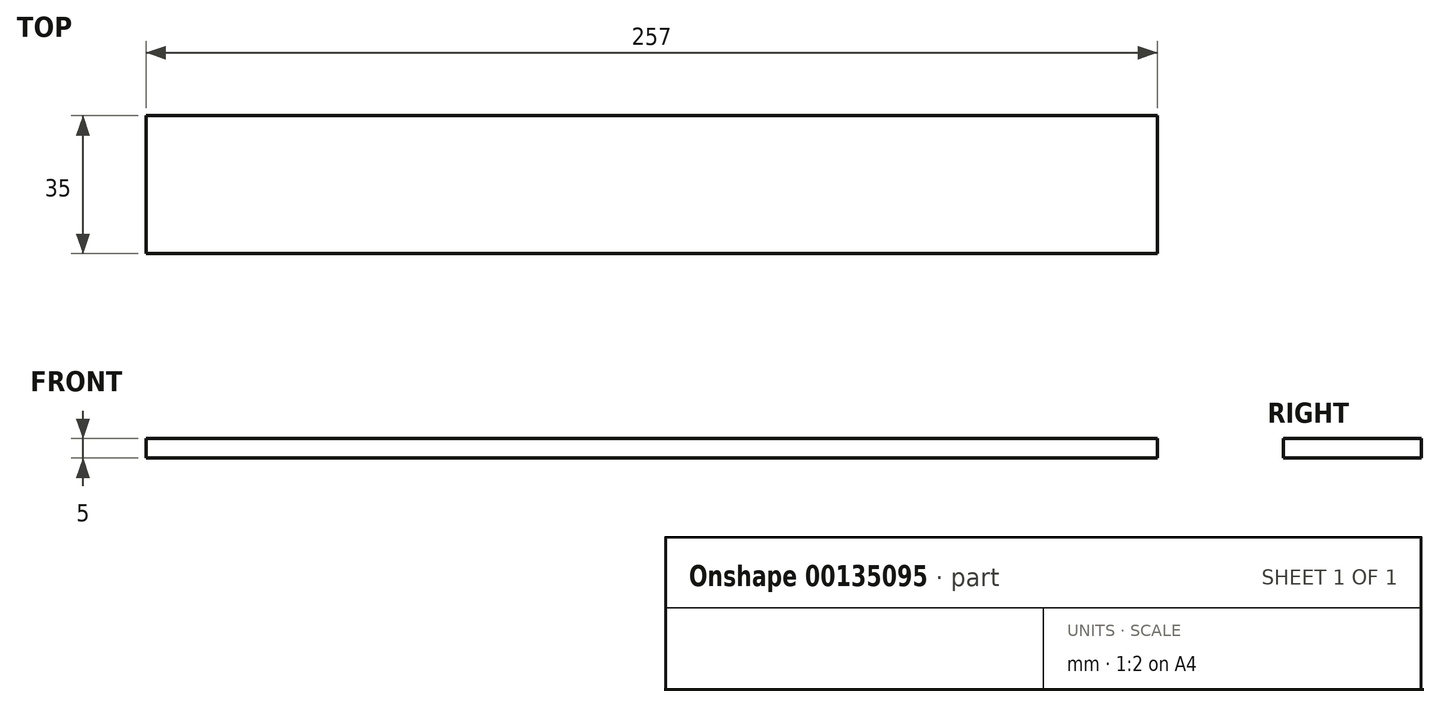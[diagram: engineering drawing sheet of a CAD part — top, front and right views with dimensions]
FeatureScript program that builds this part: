
annotation { "Feature Type Name" : "Feature", "Feature Type Description" : "" }
export const myFeature = defineFeature(function(context is Context, id is Id, definition is map)
    precondition{}
    {
        {
            var Q0;
            Q0=qCreatedBy(makeId("Top.planeOp"),FACE);
            var sketch = newSketch(context, id + "F0", { "sketchPlane" : qUnion([Q0])});
            skLineSegment(sketch, "E0.bottom", {"start": v(-76.55, 0) * mm, "end": v(220.45, 0) * mm});
            skLineSegment(sketch, "E0.top", {"start": v(-76.55, 35) * mm, "end": v(220.45, 35) * mm});
            skLineSegment(sketch, "E0.left", {"start": v(-76.55, 0) * mm, "end": v(-76.55, 35) * mm});
            skLineSegment(sketch, "E0.right", {"start": v(220.45, 0) * mm, "end": v(220.45, 35) * mm});
            skSolve(sketch);
        }
        {
            var Q0;
            Q0=makeQuery(id+"F0.imprint","IMPRINT",FACE,{"disambiguationData":[TD([[makeQuery(id+"F0.imprint","IMPRINT",EDGE,{"derivedFrom":sQuery(id+"F0.wireOp",EDGE,"E0.bottom")}),1.0]])]});
            extrude(context, id + "F1", {"entities" : qUnion([Q0]), "depth" : 5 * mm});
        }
        {
            var Q0;
            Q0=makeQuery(id+"F1.opExtrude","SWEPT_FACE",FACE,{"disambiguationData":[OSD([sQuery(id+"F0.wireOp",EDGE,"E0.right")])]});
            extrude(context, id + "F2", {"entities" : qUnion([Q0]), "operationType" : NewBodyOperationType.REMOVE, "oppositeDirection" : true, "depth" : 40 * mm});
        }
    });
